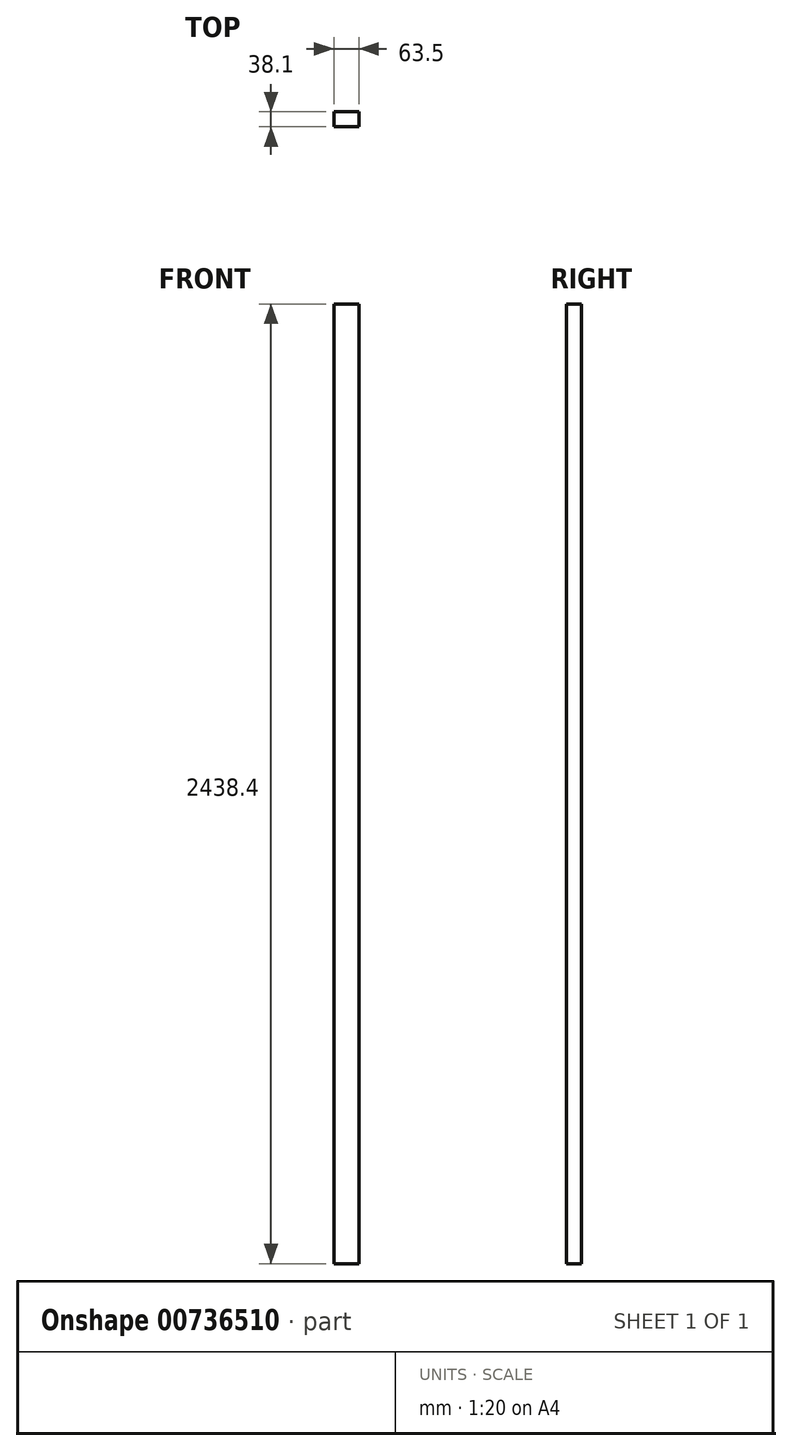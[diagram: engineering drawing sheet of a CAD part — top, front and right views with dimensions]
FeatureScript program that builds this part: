
annotation { "Feature Type Name" : "Feature", "Feature Type Description" : "" }
export const myFeature = defineFeature(function(context is Context, id is Id, definition is map)
    precondition{}
    {
        {
            var Q0;
            Q0=qCreatedBy(makeId("Top.planeOp"),FACE);
            var sketch = newSketch(context, id + "F0", { "sketchPlane" : qUnion([Q0])});
            skLineSegment(sketch, "E0.bottom", {"start": v(31.75, 19.05) * mm, "end": v(-31.75, 19.05) * mm});
            skLineSegment(sketch, "E0.top", {"start": v(31.75, -19.05) * mm, "end": v(-31.75, -19.05) * mm});
            skLineSegment(sketch, "E0.left", {"start": v(31.75, 19.05) * mm, "end": v(31.75, -19.05) * mm});
            skLineSegment(sketch, "E0.right", {"start": v(-31.75, 19.05) * mm, "end": v(-31.75, -19.05) * mm});
            skPoint(sketch, "E0.middle", {"position": v(0, 0) * mm});
            skSolve(sketch);
        }
        {
            var Q0;
            Q0 = qSketchRegion(id + "F0", true);
            extrude(context, id + "F1", {"entities" : qUnion([Q0]), "depth" : 2438.4 * mm, "offsetDistance" : 25.4 * mm});
        }
    });
